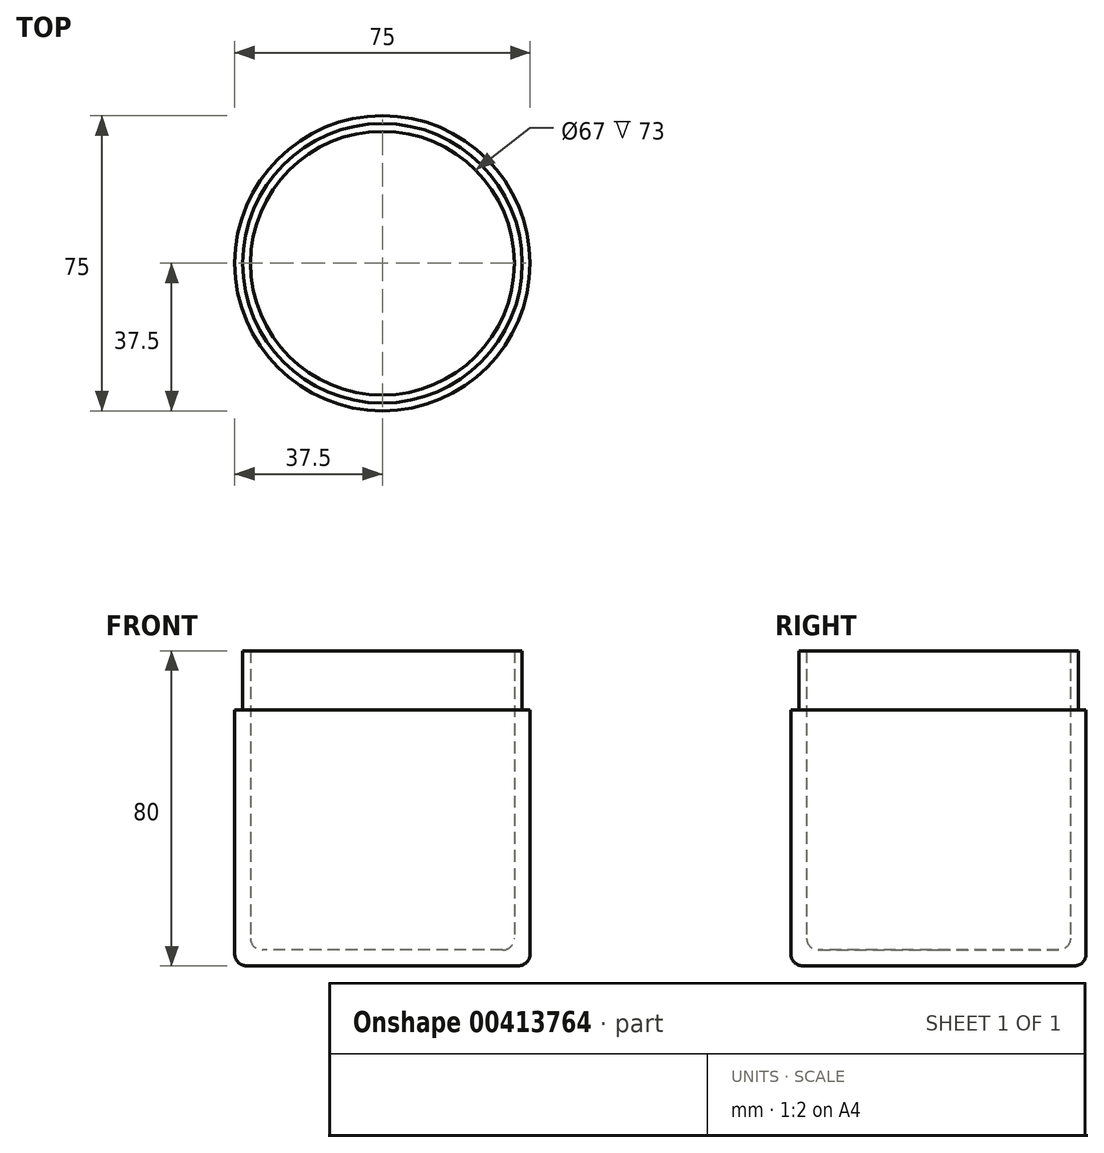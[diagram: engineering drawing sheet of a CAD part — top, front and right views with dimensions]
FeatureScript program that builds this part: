
annotation { "Feature Type Name" : "Feature", "Feature Type Description" : "" }
export const myFeature = defineFeature(function(context is Context, id is Id, definition is map)
    precondition{}
    {
        {
            var Q0;
            Q0=qCreatedBy(makeId("Top.planeOp"),FACE);
            var sketch = newSketch(context, id + "F0", { "sketchPlane" : qUnion([Q0])});
            skCircle(sketch, "E0", {"center": v(0, 0) * mm, "radius": 37.5 * mm});
            skSolve(sketch);
        }
        {
            var Q0;
            Q0 = qSketchRegion(id + "F0", true);
            extrude(context, id + "F1", {"entities" : qUnion([Q0]), "depth" : 80 * mm});
        }
        {
            var Q0;
            Q0=makeQuery(id+"F1.opExtrude","CAP_FACE",FACE,{"disambiguationData":[OSD([sQuery(id+"F0.wireOp",EDGE,"E0")])],"isStart":false});
            shell(context, id + "F2", {"entities" : qUnion([Q0]), "thickness" : 4 * mm});
        }
        {
            var Q0;
            Q0=makeQuery(id+"F1.opExtrude","CAP_FACE",FACE,{"disambiguationData":[OSD([sQuery(id+"F0.wireOp",EDGE,"E0")])],"isStart":false});
            var sketch = newSketch(context, id + "F3", { "sketchPlane" : qUnion([Q0])});
            skCircle(sketch, "E1", {"center": v(0, 0) * mm, "radius": 35.5 * mm});
            skSolve(sketch);
        }
        {
            var Q0;
            Q0=makeQuery(id+"F3.imprint","IMPRINT",FACE,{"disambiguationData":[TD([[makeQuery(id+"F3.imprint","IMPRINT",EDGE,{"derivedFrom":sQuery(id+"F3.wireOp",EDGE,"E1")}),-1.0]])]});
            extrude(context, id + "F4", {"entities" : qUnion([Q0]), "operationType" : NewBodyOperationType.REMOVE, "oppositeDirection" : true, "depth" : 15 * mm});
        }
        {
            var Q0;
            Q0=makeQuery(id+"F1.opExtrude","CAP_FACE",FACE,{"disambiguationData":[OSD([sQuery(id+"F0.wireOp",EDGE,"E0")])],"isStart":true});
            var Q1;
            {var subQ0=sQuery(id+"F0.wireOp",EDGE,"E0");Q1=makeQuery(id+"F2.opShell","OFFSET_FACE",FACE,{"disambiguationData":[OSD([subQ0]),TDD([makeQuery(id+"F1.opExtrude","CAP_FACE",FACE,{"disambiguationData":[OSD([subQ0])],"isStart":true})])]});}
            fillet(context, id + "F5", {"entities" : qUnion([Q0, Q1]), "radius" : 3 * mm, "tangentPropagation" : true, "allowEdgeOverflow" : false});
        }
    });
